# Revit family: Building-IEC309Connections-GEWISS-IEC309HP-10°_SURFACE-MOUNT_SOCKET_16A_IP44
name_source: partatom
category: Apparecchi elettrici
units: mm (PartAtom-declared; Revit-internal decimal feet)

## family parameters
Condiviso = Sì
Host = Superficie
Mantenere orientamento annotazione = Sì
Punto di calcolo locali = Sì
Quota connettore circolare = Usa diametro
Taglio con vuoti quando caricato = No
Tipo di parte = Normale

## types (11) — shared parameters
BLOCCO = B=C
Breaking capacity at 1.1 Un = 20A
Catalogue = BUILDING
Corpo centrale = Default(2)
Electrocod = 2210
FORMULA = 1000 mm  [stored 3.28084 ft]
Frequency = 50/60 Hz
Glow wire test: = 850 °C (active parts) - 650 °C (passive parts)
IDF = 3e295d74-338a-4312-b8a9-e00a704bd311
IDT = 4994872c73b647d6b63d7e176105fff7
IP degree = IP44
Immagine tipo = <Nessuno>
Insulation resistance = - 10 M?
L = 155 mm
Operating temperature: = -25 +55 °C
Permissible overload = 22A
Piastra = Default(2)
Produttore = GEWISS S.p.A.
Prospetto di default = 500 mm
Rated current (A) = 16
SEO = Socket outlet
SPinotto = Default(2)
Shock resistance = IK08
Sportello_visibile = Sì
Spostamento_S = 955 mm
Technical sheet = https://www.gewiss.com
Terminal tightening capacity = 1-2.5mm² flexible cables - 1.5-4mm² rigid cables
Thermo-pressure with ball = 125 °C (active parts) - 80 °C (passive parts)
Total number of operations = -5000
Type of wiring = With screw
Typology = 10° angled surface-mounting socket-outlet
URL = https://www.gewiss.com
Version file RFA = 21.11
W = 115 mm

## per-type parameters (varying)
| type | Colour: | Descrizione | Modello | No. of poles | Rated voltage | Reference h |
| GW62403 - IP44 10°W.RECEPTACLE 3P+N+T 16A 110V 4H | Yellow | IP44 10°W.RECEPTACLE 3P+N+T 16A 110V 4H | GW62403 | 3P+N+E | 100-130V | 4 |
| GW62401 - IP44 10°W.RECEPTACLE 2P+E 16A 110V 4H | Yellow | IP44 10°W.RECEPTACLE 2P+E 16A 110V 4H | GW62401 | 2P+E | 100-130V | 4 |
| GW62411 - IP44 10°W.RECEPTACLE 3P+N+T 16A 500V 7H | Black | IP44 10°W.RECEPTACLE 3P+N+T 16A 500V 7H | GW62411 | 3P+N+E | 480-500V | 7 |
| GW62410 - IP44 10°W.RECEPTACLE 3P+E 16A 500V 7H | Black | IP44 10°W.RECEPTACLE 3P+E 16A 500V 7H | GW62410 | 3P+E | 480-500V | 7 |
| GW62408 - IP44 10°W.RECEPTACLE 3P+E 16A 400V 6H | Red | IP44 10°W.RECEPTACLE 3P+E 16A 400V 6H | GW62408 | 3P+E | 380-415V | 6 |
| GW62404 - IP44 10°W.RECEPTACLE 2P+E 16A 230V 6H | Blue | IP44 10°W.RECEPTACLE 2P+E 16A 230V 6H | GW62404 | 2P+E | 200-250V | 6 |
| GW62409 - IP44 10°W.RECEPTACLE 3P+N+T 16A 400V 6H | Red | IP44 10°W.RECEPTACLE 3P+N+T 16A 400V 6H | GW62409 | 3P+N+E | 380-415V | 6 |
| GW62402 - IP44 10°W.RECEPTACLE 3P+E 16A 110V 4H | Yellow | IP44 10°W.RECEPTACLE 3P+E 16A 110V 4H | GW62402 | 3P+E | 100-130V | 4 |
| GW62406 - IP44 10°W.RECEPTACLE 3P+N+T 16A 230V 9H | Blue | IP44 10°W.RECEPTACLE 3P+N+T 16A 230V 9H | GW62406 | 3P+N+E | 200-250V | 9 |
| GW62407 - IP44 10°W.RECEPTACLE 2P+E 16A 400V 9H | Red | IP44 10°W.RECEPTACLE 2P+E 16A 400V 9H | GW62407 | 2P+E | 380-415V | 9 |
| GW62405 - IP44 10°W.RECEPTACLE 3P+E 16A 230V 9H | Blue | IP44 10°W.RECEPTACLE 3P+E 16A 230V 9H | GW62405 | 3P+E | 200-250V | 9 |

note: [stored X ft] marks values corroborated as IEEE doubles in the binary element streams (Revit-internal decimal feet)

## geometry (parser evidence)
native form markers: Sweep x1
no freeform markers — native parametric forms only
